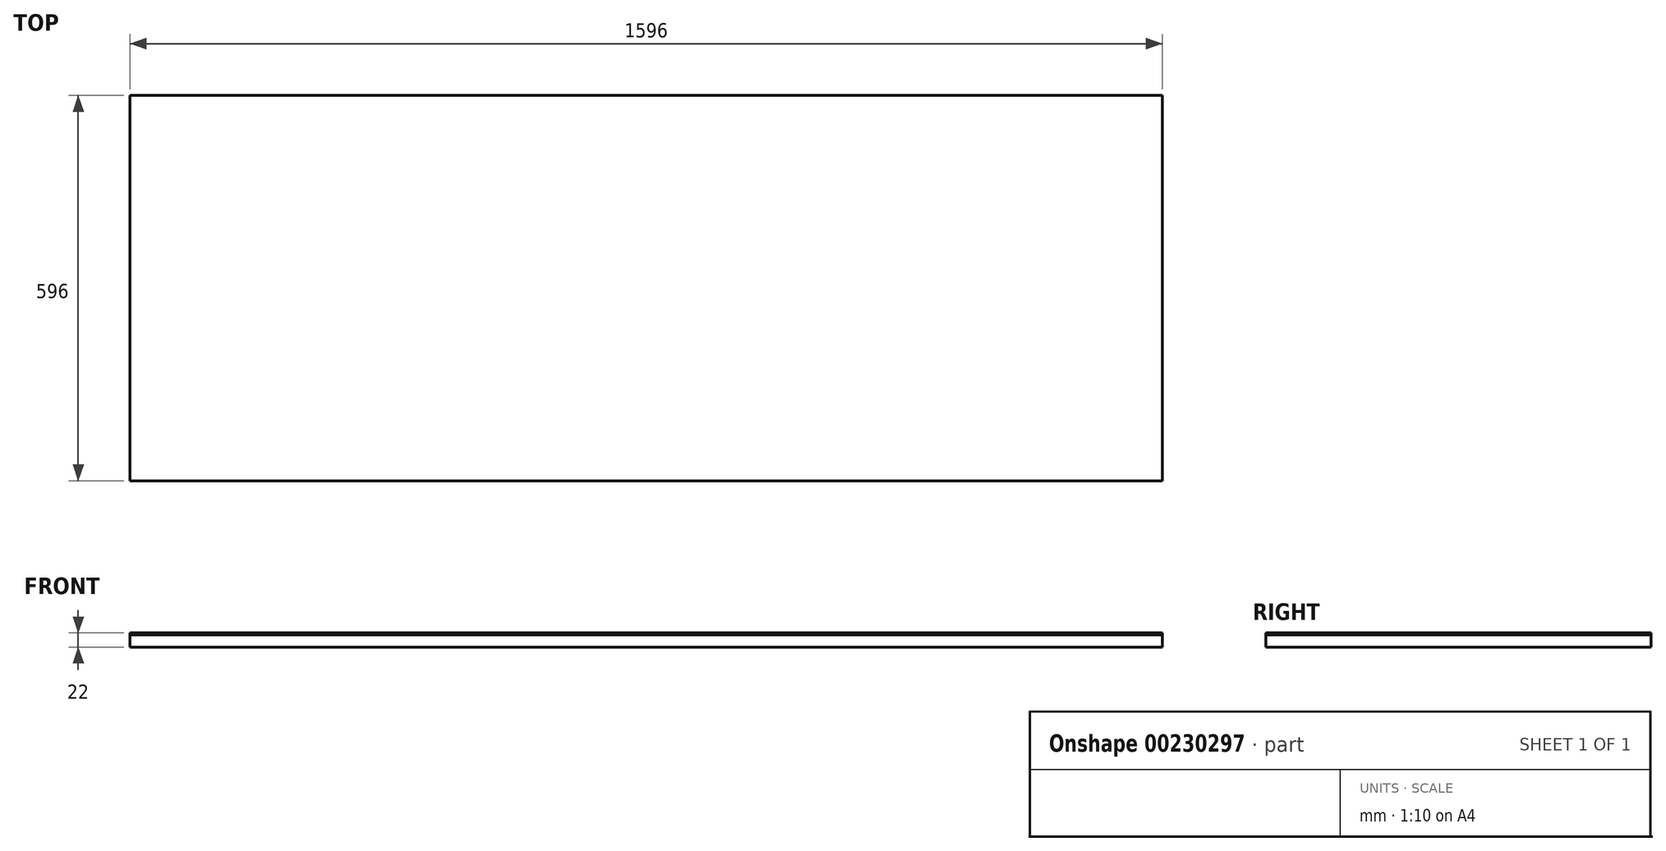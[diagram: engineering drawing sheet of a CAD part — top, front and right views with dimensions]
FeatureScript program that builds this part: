
annotation { "Feature Type Name" : "Feature", "Feature Type Description" : "" }
export const myFeature = defineFeature(function(context is Context, id is Id, definition is map)
    precondition{}
    {
        {
            var Q0;
            Q0=qCreatedBy(makeId("Top.planeOp"),FACE);
            var sketch = newSketch(context, id + "F0", { "sketchPlane" : qUnion([Q0])});
            skLineSegment(sketch, "E0.bottom", {"start": v(0, 0) * mm, "end": v(1596, 0) * mm});
            skLineSegment(sketch, "E0.top", {"start": v(0, 596) * mm, "end": v(1596, 596) * mm});
            skLineSegment(sketch, "E0.left", {"start": v(0, 0) * mm, "end": v(0, 596) * mm});
            skLineSegment(sketch, "E0.right", {"start": v(1596, 0) * mm, "end": v(1596, 596) * mm});
            skSolve(sketch);
        }
        {
            var Q0;
            Q0=makeQuery(id+"F0.imprint","IMPRINT",FACE,{"disambiguationData":[TD([[makeQuery(id+"F0.imprint","IMPRINT",EDGE,{"derivedFrom":sQuery(id+"F0.wireOp",EDGE,"E0.bottom")}),1.0]])]});
            extrude(context, id + "F1", {"entities" : qUnion([Q0]), "oppositeDirection" : true, "depth" : 19 * mm});
        }
        {
            var Q0;
            Q0 = qSketchRegion(id + "F0", true);
            extrude(context, id + "F2", {"entities" : qUnion([Q0]), "depth" : 3 * mm});
        }
    });
